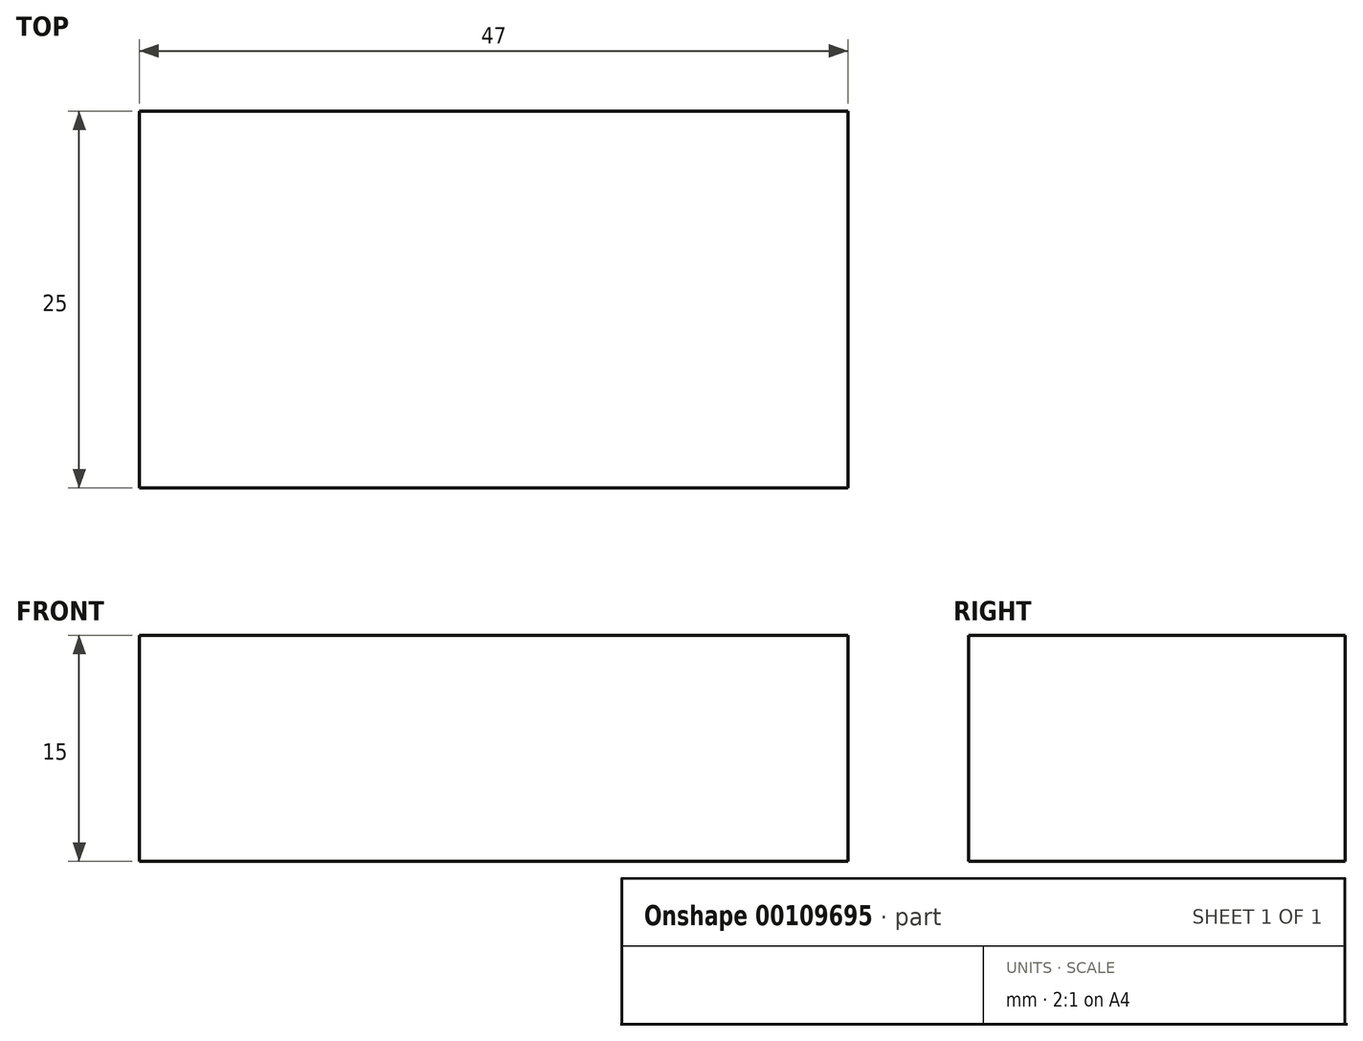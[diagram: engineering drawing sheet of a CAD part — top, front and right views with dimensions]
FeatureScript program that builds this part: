
annotation { "Feature Type Name" : "Feature", "Feature Type Description" : "" }
export const myFeature = defineFeature(function(context is Context, id is Id, definition is map)
    precondition{}
    {
        {
            var Q0;
            Q0=qCreatedBy(makeId("Top.planeOp"),FACE);
            var sketch = newSketch(context, id + "F0", { "sketchPlane" : qUnion([Q0])});
            skLineSegment(sketch, "E0", {"start": v(0, 0) * mm, "end": v(47, 0) * mm});
            skLineSegment(sketch, "E1", {"start": v(0, 0) * mm, "end": v(0, 25) * mm});
            skLineSegment(sketch, "E2", {"start": v(0, 25) * mm, "end": v(47, 25) * mm});
            skLineSegment(sketch, "E3", {"start": v(47, 25) * mm, "end": v(47, 0) * mm});
            skSolve(sketch);
        }
        {
            var Q0;
            Q0 = qSketchRegion(id + "F0", true);
            extrude(context, id + "F1", {"entities" : qUnion([Q0]), "depth" : 15 * mm});
        }
    });
